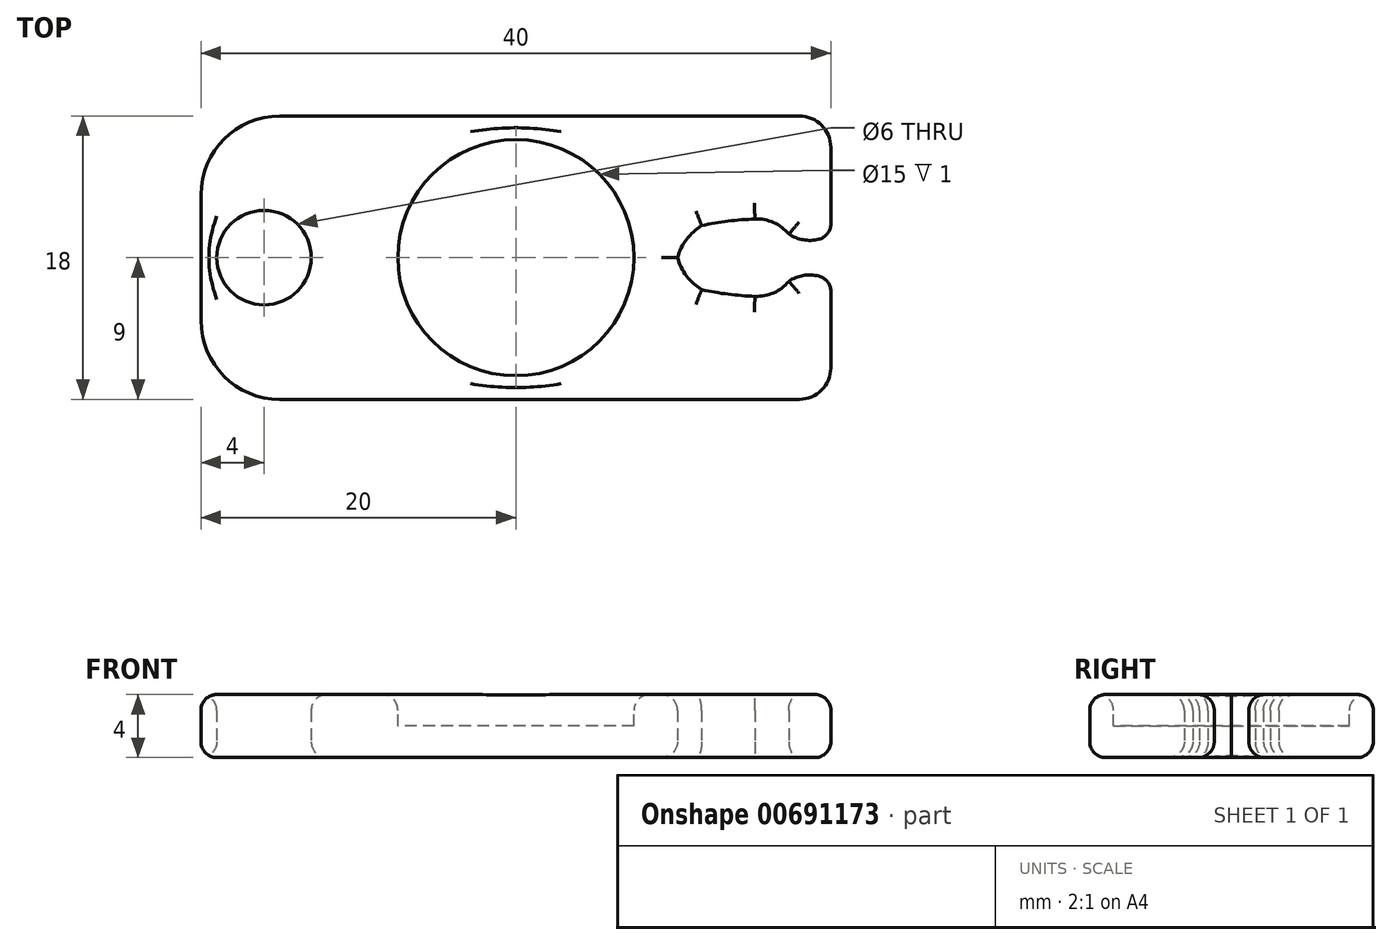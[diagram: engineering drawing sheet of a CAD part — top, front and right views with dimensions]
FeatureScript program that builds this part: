
annotation { "Feature Type Name" : "Feature", "Feature Type Description" : "" }
export const myFeature = defineFeature(function(context is Context, id is Id, definition is map)
    precondition{}
    {
        {
            var Q0;
            Q0=qCreatedBy(makeId("Top.planeOp"),FACE);
            var sketch = newSketch(context, id + "F0", { "sketchPlane" : qUnion([Q0])});
            skLineSegment(sketch, "E0", {"start": v(-10, 0) * mm, "end": v(-9, 0) * mm, "construction": true});
            skLineSegment(sketch, "E1", {"start": v(0, 25.88) * mm, "end": v(0, 0) * mm, "construction": true});
            skLineSegment(sketch, "E2", {"start": v(-10, 0) * mm, "end": v(-10, 4) * mm});
            skLineSegment(sketch, "E3", {"start": v(-5, 9) * mm, "end": v(28, 9) * mm});
            skLineSegment(sketch, "E4", {"start": v(30, 7) * mm, "end": v(30, 1.5) * mm});
            skLineSegment(sketch, "E5", {"start": v(-10, 0) * mm, "end": v(-9, 0) * mm});
            skPoint(sketch, "E6.visualSharp", {"position": v(-10, 9) * mm});
            skArc(sketch, "E6.filletArc", {"start": v(-5, 9) * mm, "mid": v(-8.54, 7.54) * mm, "end": v(-10, 4) * mm});
            skPoint(sketch, "E7.visualSharp", {"position": v(30, 9) * mm});
            skArc(sketch, "E7.filletArc", {"start": v(30, 7) * mm, "mid": v(29.41, 8.41) * mm, "end": v(28, 9) * mm});
            skArc(sketch, "E8", {"start": v(-3, 0) * mm, "mid": v(-6, 3) * mm, "end": v(-9, 0) * mm});
            skPoint(sketch, "E9.orphan", {"position": v(-40.04, 0) * mm});
            skLineSegment(sketch, "E10.trimOffspring", {"start": v(-3, 0) * mm, "end": v(5, 0) * mm, "construction": true});
            skLineSegment(sketch, "E11.trimOffspring", {"start": v(-3, 0) * mm, "end": v(5, 0) * mm});
            skArc(sketch, "E12.MirrorCS", {"start": v(30, -7) * mm, "mid": v(29.41, -8.41) * mm, "end": v(28, -9) * mm});
            skArc(sketch, "E13.MirrorCS", {"start": v(-5, -9) * mm, "mid": v(-8.54, -7.54) * mm, "end": v(-10, -4) * mm});
            skPoint(sketch, "E14.MirrorP", {"position": v(30, -9) * mm});
            skPoint(sketch, "E15.MirrorP", {"position": v(-10, -9) * mm});
            skLineSegment(sketch, "E16.MirrorCS", {"start": v(30, -7) * mm, "end": v(30, -1.5) * mm});
            skLineSegment(sketch, "E17.MirrorCS", {"start": v(-5, -9) * mm, "end": v(28, -9) * mm});
            skArc(sketch, "E18.MirrorCS", {"start": v(-3, 0) * mm, "mid": v(-6, -3) * mm, "end": v(-9, 0) * mm});
            skLineSegment(sketch, "E19.MirrorCS", {"start": v(-10, 0) * mm, "end": v(-10, -4) * mm});
            skPoint(sketch, "E20.MirrorCS.end.orphan", {"position": v(5, 0) * mm});
            skPoint(sketch, "E20.MirrorCS.start.orphan", {"position": v(30, -1.5) * mm});
            skLineSegment(sketch, "E21", {"start": v(38.43, 0) * mm, "end": v(0, 0) * mm, "construction": true});
            skArc(sketch, "E22", {"start": v(27.33, 1.5) * mm, "mid": v(28.66, 1.1) * mm, "end": v(30, 1.5) * mm});
            skArc(sketch, "E23", {"start": v(27.33, 1.5) * mm, "mid": v(26.37, 2.23) * mm, "end": v(25.18, 2.45) * mm});
            skArc(sketch, "E24", {"start": v(25.18, 2.45) * mm, "mid": v(23.48, 2.32) * mm, "end": v(21.8, 2.03) * mm});
            skArc(sketch, "E25", {"start": v(21.8, 2.03) * mm, "mid": v(20.84, 1.16) * mm, "end": v(20.27, 0) * mm});
            skArc(sketch, "E26.MirrorCS", {"start": v(27.33, -1.5) * mm, "mid": v(28.66, -1.1) * mm, "end": v(30, -1.5) * mm});
            skArc(sketch, "E27.MirrorCS", {"start": v(27.33, -1.5) * mm, "mid": v(26.37, -2.23) * mm, "end": v(25.18, -2.45) * mm});
            skArc(sketch, "E28.MirrorCS", {"start": v(25.18, -2.45) * mm, "mid": v(23.48, -2.32) * mm, "end": v(21.8, -2.03) * mm});
            skArc(sketch, "E29.MirrorCS", {"start": v(21.8, -2.03) * mm, "mid": v(20.84, -1.16) * mm, "end": v(20.27, 0) * mm});
            skPoint(sketch, "E30.MirrorP", {"position": v(30, 1.5) * mm});
            skSolve(sketch);
        }
        {
            var Q0;
            Q0=makeQuery(id+"F0.imprint","IMPRINT",FACE,{"disambiguationData":[TD([[makeQuery(id+"F0.imprint","IMPRINT",EDGE,{"derivedFrom":sQuery(id+"F0.wireOp",EDGE,"E2")}),-1.0]])]});
            extrude(context, id + "F1", {"entities" : qUnion([Q0]), "depth" : 4 * mm, "offsetDistance" : 25 * mm});
        }
        {
            var Q0;
            Q0=makeQuery(id+"F1.opExtrude","CAP_FACE",FACE,{"disambiguationData":[OSD([sQuery(id+"F0.wireOp",EDGE,"E2"),sQuery(id+"F0.wireOp",EDGE,"E6.filletArc"),sQuery(id+"F0.wireOp",EDGE,"E8"),sQuery(id+"F0.wireOp",EDGE,"E13.MirrorCS"),sQuery(id+"F0.wireOp",EDGE,"E18.MirrorCS"),sQuery(id+"F0.wireOp",EDGE,"E19.MirrorCS"),sQuery(id+"F0.wireOp",EDGE,"E26.MirrorCS"),sQuery(id+"F0.wireOp",EDGE,"E7.filletArc"),sQuery(id+"F0.wireOp",EDGE,"E4"),sQuery(id+"F0.wireOp",EDGE,"E24"),sQuery(id+"F0.wireOp",EDGE,"E12.MirrorCS"),sQuery(id+"F0.wireOp",EDGE,"E27.MirrorCS"),sQuery(id+"F0.wireOp",EDGE,"E28.MirrorCS"),sQuery(id+"F0.wireOp",EDGE,"E22"),sQuery(id+"F0.wireOp",EDGE,"E23"),sQuery(id+"F0.wireOp",EDGE,"E16.MirrorCS"),sQuery(id+"F0.wireOp",EDGE,"E29.MirrorCS"),sQuery(id+"F0.wireOp",EDGE,"E3"),sQuery(id+"F0.wireOp",EDGE,"E25"),sQuery(id+"F0.wireOp",EDGE,"E17.MirrorCS")])],"isStart":false});
            var sketch = newSketch(context, id + "F2", { "sketchPlane" : qUnion([Q0])});
            skLineSegment(sketch, "E31", {"start": v(-0.25, 0) * mm, "end": v(36.23, 0) * mm, "construction": true});
            skCircle(sketch, "E32", {"center": v(10, 0) * mm, "radius": 7.5 * mm});
            skSolve(sketch);
        }
        {
            var Q0;
            Q0=makeQuery(id+"F2.imprint","IMPRINT",FACE,{"disambiguationData":[TD([[makeQuery(id+"F2.imprint","IMPRINT",EDGE,{"derivedFrom":sQuery(id+"F2.wireOp",EDGE,"E32")}),1.0]])]});
            extrude(context, id + "F3", {"entities" : qUnion([Q0]), "operationType" : NewBodyOperationType.REMOVE, "oppositeDirection" : true, "depth" : 2 * mm, "offsetDistance" : 25 * mm});
        }
        {
            var Q0;
            Q0=makeQuery(id+"F1.opExtrude","SWEPT_EDGE",EDGE,{"disambiguationData":[OSD([sQuery(id+"F0.wireOp",EDGE,"E4"),sQuery(id+"F0.wireOp",EDGE,"E22")])]});
            var Q1;
            Q1=makeQuery(id+"F1.opExtrude","SWEPT_EDGE",EDGE,{"disambiguationData":[OSD([sQuery(id+"F0.wireOp",EDGE,"E26.MirrorCS"),sQuery(id+"F0.wireOp",EDGE,"E16.MirrorCS")])]});
            var Q2;
            Q2=makeQuery(id+"F1.opExtrude","CAP_FACE",FACE,{"disambiguationData":[OSD([sQuery(id+"F0.wireOp",EDGE,"E2"),sQuery(id+"F0.wireOp",EDGE,"E6.filletArc"),sQuery(id+"F0.wireOp",EDGE,"E8"),sQuery(id+"F0.wireOp",EDGE,"E13.MirrorCS"),sQuery(id+"F0.wireOp",EDGE,"E18.MirrorCS"),sQuery(id+"F0.wireOp",EDGE,"E19.MirrorCS"),sQuery(id+"F0.wireOp",EDGE,"E26.MirrorCS"),sQuery(id+"F0.wireOp",EDGE,"E7.filletArc"),sQuery(id+"F0.wireOp",EDGE,"E4"),sQuery(id+"F0.wireOp",EDGE,"E24"),sQuery(id+"F0.wireOp",EDGE,"E12.MirrorCS"),sQuery(id+"F0.wireOp",EDGE,"E27.MirrorCS"),sQuery(id+"F0.wireOp",EDGE,"E28.MirrorCS"),sQuery(id+"F0.wireOp",EDGE,"E22"),sQuery(id+"F0.wireOp",EDGE,"E23"),sQuery(id+"F0.wireOp",EDGE,"E16.MirrorCS"),sQuery(id+"F0.wireOp",EDGE,"E29.MirrorCS"),sQuery(id+"F0.wireOp",EDGE,"E3"),sQuery(id+"F0.wireOp",EDGE,"E25"),sQuery(id+"F0.wireOp",EDGE,"E17.MirrorCS")])],"isStart":false});
            var Q3;
            Q3=makeQuery(id+"F1.opExtrude","CAP_FACE",FACE,{"disambiguationData":[OSD([sQuery(id+"F0.wireOp",EDGE,"E2"),sQuery(id+"F0.wireOp",EDGE,"E6.filletArc"),sQuery(id+"F0.wireOp",EDGE,"E8"),sQuery(id+"F0.wireOp",EDGE,"E13.MirrorCS"),sQuery(id+"F0.wireOp",EDGE,"E18.MirrorCS"),sQuery(id+"F0.wireOp",EDGE,"E19.MirrorCS"),sQuery(id+"F0.wireOp",EDGE,"E26.MirrorCS"),sQuery(id+"F0.wireOp",EDGE,"E7.filletArc"),sQuery(id+"F0.wireOp",EDGE,"E4"),sQuery(id+"F0.wireOp",EDGE,"E24"),sQuery(id+"F0.wireOp",EDGE,"E12.MirrorCS"),sQuery(id+"F0.wireOp",EDGE,"E27.MirrorCS"),sQuery(id+"F0.wireOp",EDGE,"E28.MirrorCS"),sQuery(id+"F0.wireOp",EDGE,"E22"),sQuery(id+"F0.wireOp",EDGE,"E23"),sQuery(id+"F0.wireOp",EDGE,"E16.MirrorCS"),sQuery(id+"F0.wireOp",EDGE,"E29.MirrorCS"),sQuery(id+"F0.wireOp",EDGE,"E3"),sQuery(id+"F0.wireOp",EDGE,"E25"),sQuery(id+"F0.wireOp",EDGE,"E17.MirrorCS")])],"isStart":true});
            fillet(context, id + "F4", {"entities" : qUnion([Q0, Q1, Q2, Q3]), "radius" : 1 * mm, "tangentPropagation" : true, "allowEdgeOverflow" : false});
        }
    });
